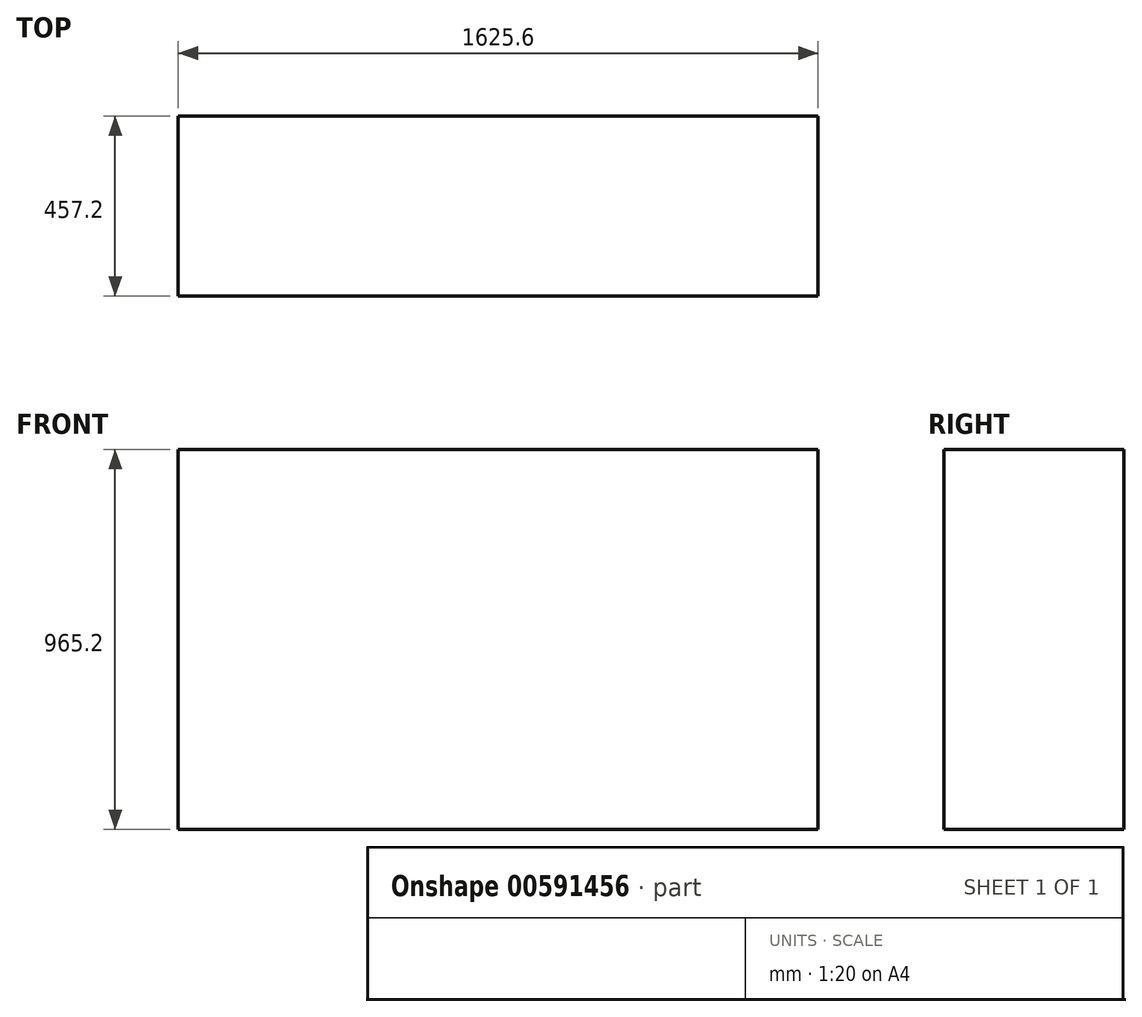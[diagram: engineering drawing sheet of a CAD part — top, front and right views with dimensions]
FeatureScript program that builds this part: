
annotation { "Feature Type Name" : "Feature", "Feature Type Description" : "" }
export const myFeature = defineFeature(function(context is Context, id is Id, definition is map)
    precondition{}
    {
        {
            var Q0;
            Q0=qCreatedBy(makeId("Front.planeOp"),FACE);
            var sketch = newSketch(context, id + "F0", { "sketchPlane" : qUnion([Q0])});
            skLineSegment(sketch, "E0.bottom", {"start": v(-806.16, 507.1) * mm, "end": v(819.44, 507.1) * mm});
            skLineSegment(sketch, "E0.top", {"start": v(-806.16, -458.1) * mm, "end": v(819.44, -458.1) * mm});
            skLineSegment(sketch, "E0.left", {"start": v(-806.16, 507.1) * mm, "end": v(-806.16, -458.1) * mm});
            skLineSegment(sketch, "E0.right", {"start": v(819.44, 507.1) * mm, "end": v(819.44, -458.1) * mm});
            skSolve(sketch);
        }
        {
            var Q0;
            Q0=makeQuery(id+"F0.imprint","IMPRINT",FACE,{"disambiguationData":[TD([[makeQuery(id+"F0.imprint","IMPRINT",EDGE,{"derivedFrom":sQuery(id+"F0.wireOp",EDGE,"E0.bottom")}),-1.0]])]});
            extrude(context, id + "F1", {"entities" : qUnion([Q0]), "endBound" : BoundingType.SYMMETRIC, "depth" : 457.2 * mm, "offsetDistance" : 25.4 * mm});
        }
    });
